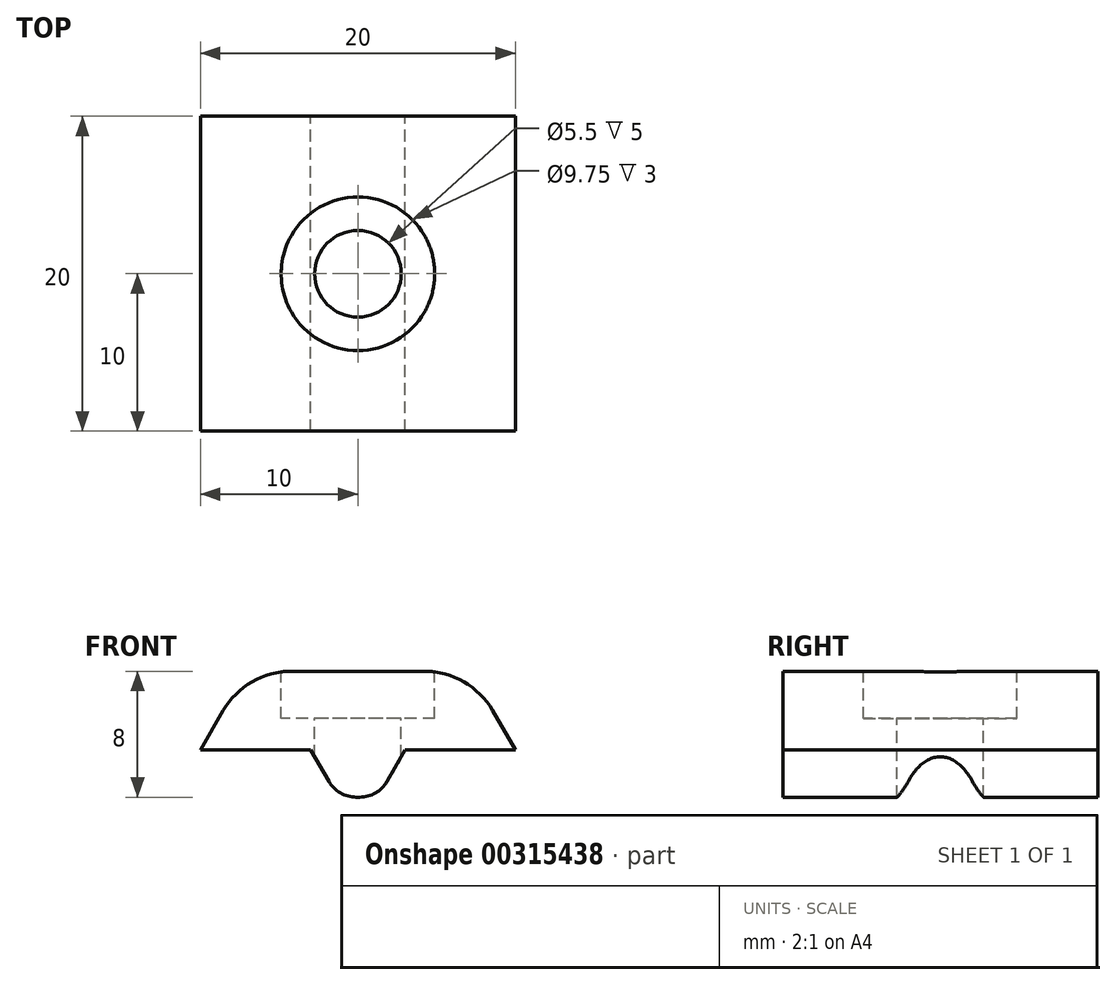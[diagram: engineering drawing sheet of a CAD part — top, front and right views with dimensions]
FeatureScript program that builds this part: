
annotation { "Feature Type Name" : "Feature", "Feature Type Description" : "" }
export const myFeature = defineFeature(function(context is Context, id is Id, definition is map)
    precondition{}
    {
        {
            var Q0;
            Q0=qCreatedBy(makeId("Front.planeOp"),FACE);
            var sketch = newSketch(context, id + "F0", { "sketchPlane" : qUnion([Q0])});
            skLineSegment(sketch, "E0", {"start": v(-10, 0) * mm, "end": v(-3, 0) * mm});
            skLineSegment(sketch, "E1", {"start": v(-3, 0) * mm, "end": v(-1.27, -3) * mm});
            skLineSegment(sketch, "E2", {"start": v(-1.27, -3) * mm, "end": v(1.27, -3) * mm});
            skLineSegment(sketch, "E3", {"start": v(1.27, -3) * mm, "end": v(3, 0) * mm});
            skLineSegment(sketch, "E4", {"start": v(3, 0) * mm, "end": v(10, 0) * mm});
            skLineSegment(sketch, "E5", {"start": v(10, 0) * mm, "end": v(7.11, 5) * mm});
            skLineSegment(sketch, "E6", {"start": v(7.11, 5) * mm, "end": v(-7.11, 5) * mm});
            skLineSegment(sketch, "E7", {"start": v(-7.11, 5) * mm, "end": v(-10, 0) * mm});
            skSolve(sketch);
        }
        {
            var Q0;
            Q0 = qSketchRegion(id + "F0", true);
            extrude(context, id + "F1", {"entities" : qUnion([Q0]), "depth" : 20 * mm});
        }
        {
            var Q0;
            Q0=makeQuery(id+"F1.opExtrude","SWEPT_EDGE",EDGE,{"disambiguationData":[OSD([sQuery(id+"F0.wireOp",EDGE,"E5"),sQuery(id+"F0.wireOp",EDGE,"E6")])]});
            var Q1;
            Q1=makeQuery(id+"F1.opExtrude","SWEPT_EDGE",EDGE,{"disambiguationData":[OSD([sQuery(id+"F0.wireOp",EDGE,"E6"),sQuery(id+"F0.wireOp",EDGE,"E7")])]});
            fillet(context, id + "F2", {"entities" : qUnion([Q0, Q1]), "radius" : 5 * mm, "tangentPropagation" : true, "allowEdgeOverflow" : false});
        }
        {
            var Q0;
            Q0=makeQuery(id+"F1.opExtrude","SWEPT_EDGE",EDGE,{"disambiguationData":[OSD([sQuery(id+"F0.wireOp",EDGE,"E2"),sQuery(id+"F0.wireOp",EDGE,"E3")])]});
            var Q1;
            Q1=makeQuery(id+"F1.opExtrude","SWEPT_EDGE",EDGE,{"disambiguationData":[OSD([sQuery(id+"F0.wireOp",EDGE,"E1"),sQuery(id+"F0.wireOp",EDGE,"E2")])]});
            fillet(context, id + "F3", {"entities" : qUnion([Q0, Q1]), "radius" : 2 * mm, "tangentPropagation" : true, "allowEdgeOverflow" : false});
        }
        {
            var Q0;
            Q0=makeQuery(id+"F1.opExtrude","SWEPT_FACE",FACE,{"disambiguationData":[OSD([sQuery(id+"F0.wireOp",EDGE,"E6")])]});
            var sketch = newSketch(context, id + "F4", { "sketchPlane" : qUnion([Q0])});
            skPoint(sketch, "E8", {"position": v(0, -10) * mm});
            skSolve(sketch);
        }
        {
            var Q0;
            Q0=sQuery(id+"F4.wireOp",VERTEX,"E8");
            var Q1;
            Q1=makeQuery(id+"F1.opExtrude","SWEPT_BODY",BODY,{"disambiguationData":[OSD([sQuery(id+"F0.wireOp",EDGE,"E0"),sQuery(id+"F0.wireOp",EDGE,"E1"),sQuery(id+"F0.wireOp",EDGE,"E2"),sQuery(id+"F0.wireOp",EDGE,"E3"),sQuery(id+"F0.wireOp",EDGE,"E4"),sQuery(id+"F0.wireOp",EDGE,"E5"),sQuery(id+"F0.wireOp",EDGE,"E6"),sQuery(id+"F0.wireOp",EDGE,"E7")])]});
            hole(context, id + "F5", {"style" : HoleStyle.C_BORE, "endStyle" : HoleEndStyle.BLIND, "holeDiameter" : 5.5 * mm, "cBoreDiameter" : 9.75 * mm, "cBoreDepth" : 3 * mm, "holeDepth" : 30 * mm, "tappedDepth" : 12 * mm, "tapClearance" : 3, "startFromSketch" : true, "locations" : qUnion([Q0]), "scope" : qUnion([Q1])});
        }
    });
